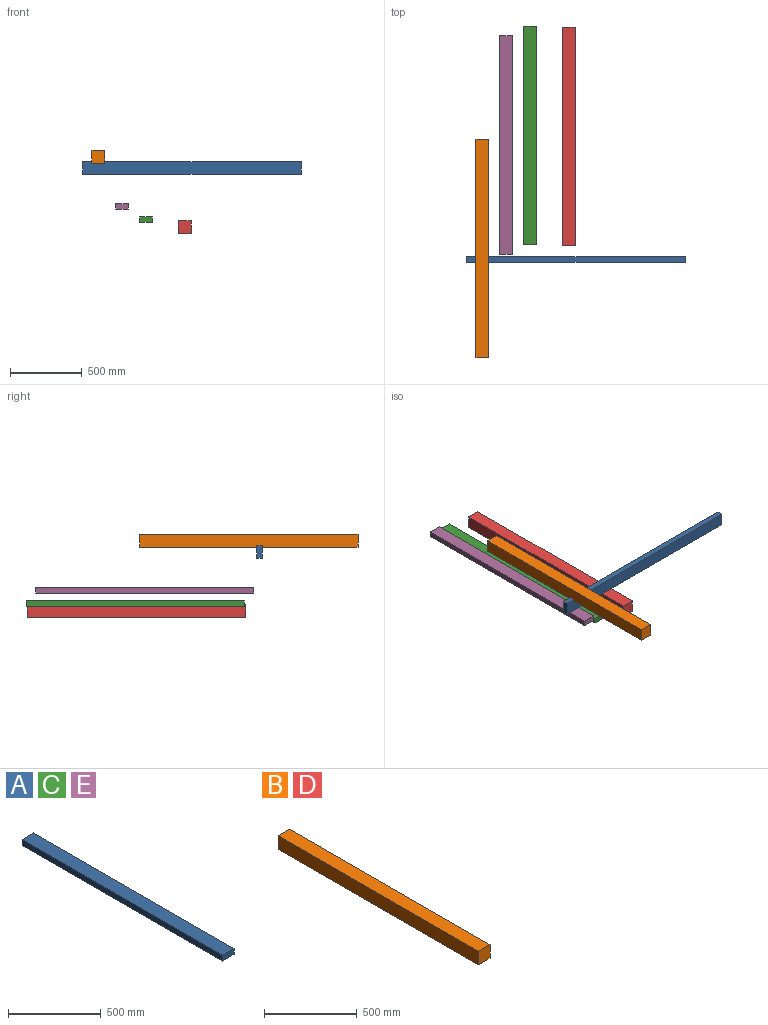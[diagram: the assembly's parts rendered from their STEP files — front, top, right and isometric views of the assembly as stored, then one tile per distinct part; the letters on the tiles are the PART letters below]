
ASSEMBLY  parts=5 mates=1
PART A: 6 faces, bbox 88.9x1524x38.1 mm
  f0: plane 1524x88.9mm, normal (0,0,-1), area 135483.6mm2, adj f1,f3,f4,f5
  f1: plane 1524x38.1mm, normal (1,0,0), area 58064.4mm2, adj f0,f2,f4,f5
  f2: plane 1524x88.9mm, normal (0,0,1), area 135483.6mm2, adj f1,f3,f4,f5
  f3: plane 1524x38.1mm, normal (-1,0,0), area 58064.4mm2, adj f0,f2,f4,f5
  f4: plane 88.9x38.1mm, normal (0,-1,0), area 3387.1mm2, adj f0,f1,f2,f3
  f5: plane 88.9x38.1mm, normal (0,1,0), area 3387.1mm2, adj f0,f1,f2,f3
PART B: 6 faces, bbox 88.9x1524x88.9 mm
  f0: plane 1524x88.9mm, normal (0,0,-1), area 135483.6mm2, adj f1,f3,f4,f5
  f1: plane 1524x88.9mm, normal (1,0,0), area 135483.6mm2, adj f0,f2,f4,f5
  f2: plane 1524x88.9mm, normal (0,0,1), area 135483.6mm2, adj f1,f3,f4,f5
  f3: plane 1524x88.9mm, normal (-1,0,0), area 135483.6mm2, adj f0,f2,f4,f5
  f4: plane 88.9x88.9mm, normal (0,-1,0), area 7903.2mm2, adj f0,f1,f2,f3
  f5: plane 88.9x88.9mm, normal (0,1,0), area 7903.2mm2, adj f0,f1,f2,f3
PART C: same geometry as A
PART D: same geometry as B
PART E: same geometry as A
PLACE A rot(axis=(0.58,0.58,-0.58),120deg) t=(1415.55,-836.87,-77.19)mm
PLACE B at identity
PLACE C t=(333.02,791.97,-438.52)mm
PLACE D t=(603.53,783.45,-490.5)mm
PLACE E t=(164.86,725.56,-345.41)mm
MATE parallel A.f4 <-> B.f1  axis (-1,0,0) through (-108.45,-836.87,-77.19)mm
